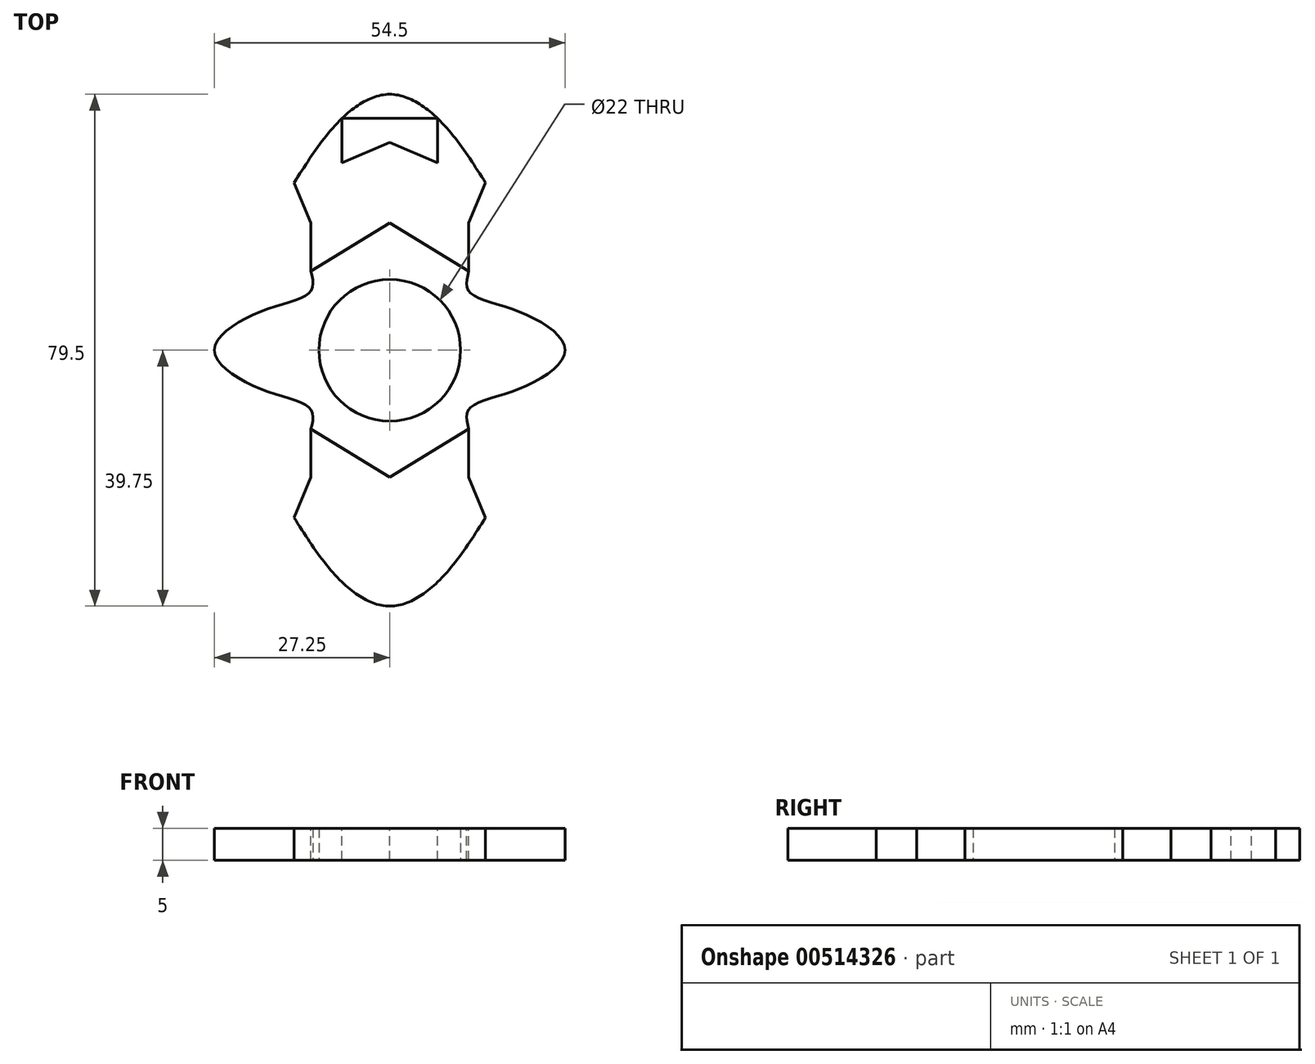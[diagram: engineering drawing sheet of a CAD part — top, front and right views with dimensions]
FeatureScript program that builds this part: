
annotation { "Feature Type Name" : "Feature", "Feature Type Description" : "" }
export const myFeature = defineFeature(function(context is Context, id is Id, definition is map)
    precondition{}
    {
        {
            var Q0;
            Q0=qCreatedBy(makeId("Top.planeOp"),FACE);
            var sketch = newSketch(context, id + "F0", { "sketchPlane" : qUnion([Q0])});
            skCircle(sketch, "E0", {"center": v(0, 0) * mm, "radius": 11 * mm});
            skCircle(sketch, "E1", {"center": v(0, 0) * mm, "radius": 12.25 * mm});
            skSolve(sketch);
        }
        {
            var Q0;
            Q0=qCreatedBy(makeId("Top.planeOp"),FACE);
            var sketch = newSketch(context, id + "F1", { "sketchPlane" : qUnion([Q0])});
            skLineSegment(sketch, "E2", {"start": v(0, 0) * mm, "end": v(-12.25, 0) * mm});
            skLineSegment(sketch, "E3", {"start": v(0, 0) * mm, "end": v(12.25, 0) * mm});
            skLineSegment(sketch, "E4", {"start": v(-12.25, 12.25) * mm, "end": v(0, 19.75) * mm});
            skLineSegment(sketch, "E5", {"start": v(0, 19.75) * mm, "end": v(12.25, 12.25) * mm});
            skLineSegment(sketch, "E6", {"start": v(-12.25, -12.25) * mm, "end": v(0, -19.75) * mm});
            skLineSegment(sketch, "E7", {"start": v(12.25, -12.25) * mm, "end": v(0, -19.75) * mm});
            skPoint(sketch, "E8.endSnap0", {"position": v(-12.25, 6.12) * mm});
            skPoint(sketch, "E9.endSnap0", {"position": v(-12.25, -6.12) * mm});
            skPoint(sketch, "E10.endSnap0", {"position": v(12.25, 6.12) * mm});
            skFitSpline(sketch, "E11", {"points": [v(-12.25, 12.25) * mm, v(-12.25, 9.19) * mm, v(-19.75, 6.12) * mm, v(-27.25, 0) * mm, v(-19.75, -6.12) * mm, v(-12.25, -9.19) * mm, v(-12.25, -12.25) * mm], "startDerivative": vector(7.59, -29.79) * mm, "endDerivative": vector(-7.59, -29.79) * mm});
            skFitSpline(sketch, "E12", {"points": [v(12.25, 12.25) * mm, v(12.25, 9.19) * mm, v(19.75, 6.12) * mm, v(27.25, 0) * mm, v(19.75, -6.12) * mm, v(12.25, -9.19) * mm, v(12.25, -12.25) * mm], "startDerivative": vector(-7.59, -29.79) * mm, "endDerivative": vector(7.59, -29.79) * mm});
            skLineSegment(sketch, "E13", {"start": v(-27.25, 0) * mm, "end": v(-12.25, 0) * mm});
            skLineSegment(sketch, "E14", {"start": v(-19.75, 0) * mm, "end": v(-12.25, 0) * mm});
            skLineSegment(sketch, "E15", {"start": v(12.25, 0) * mm, "end": v(27.25, 0) * mm});
            skLineSegment(sketch, "E16", {"start": v(19.75, 0) * mm, "end": v(12.25, 0) * mm});
            skSolve(sketch);
        }
        {
            var Q0;
            Q0=makeQuery(id+"F1.imprint","IMPRINT",FACE,{"disambiguationData":[TD([[makeQuery(id+"F1.imprint","IMPRINT",EDGE,{"derivedFrom":sQuery(id+"F1.wireOp",EDGE,"E2")}),-1.0]])]});
            var Q1;
            Q1=makeQuery(id+"F1.imprint","IMPRINT",FACE,{"disambiguationData":[TD([[makeQuery(id+"F1.imprint","IMPRINT",EDGE,{"derivedFrom":sQuery(id+"F1.wireOp",EDGE,"E2")}),1.0]])]});
            extrude(context, id + "F2", {"entities" : qUnion([Q0, Q1]), "depth" : 5 * mm, "offsetDistance" : 25 * mm});
        }
        {
            var Q0;
            Q0=makeQuery(id+"F0.imprint","IMPRINT",FACE,{"disambiguationData":[TD([[makeQuery(id+"F0.imprint","IMPRINT",EDGE,{"derivedFrom":sQuery(id+"F0.wireOp",EDGE,"E0")}),1.0]])]});
            extrude(context, id + "F3", {"entities" : qUnion([Q0]), "operationType" : NewBodyOperationType.REMOVE, "depth" : 25 * mm, "offsetDistance" : 25 * mm});
        }
        {
            var Q0;
            Q0=makeQuery(id+"F2.opExtrude","CAP_FACE",FACE,{"disambiguationData":[OSD([sQuery(id+"F1.wireOp",EDGE,"E4"),sQuery(id+"F1.wireOp",EDGE,"E5"),sQuery(id+"F1.wireOp",EDGE,"E6"),sQuery(id+"F1.wireOp",EDGE,"E7"),sQuery(id+"F1.wireOp",EDGE,"E11"),sQuery(id+"F1.wireOp",EDGE,"E12")])],"isStart":false});
            var sketch = newSketch(context, id + "F4", { "sketchPlane" : qUnion([Q0])});
            skLineSegment(sketch, "E17", {"start": v(-12.25, 12.25) * mm, "end": v(-12.25, 19.75) * mm});
            skLineSegment(sketch, "E18", {"start": v(12.25, 19.75) * mm, "end": v(12.25, 12.25) * mm});
            skLineSegment(sketch, "E19", {"start": v(0, 19.75) * mm, "end": v(0, 32.25) * mm});
            skLineSegment(sketch, "E20", {"start": v(-12.25, 19.75) * mm, "end": v(0, 32.25) * mm});
            skLineSegment(sketch, "E21", {"start": v(0, 32.25) * mm, "end": v(12.25, 19.75) * mm});
            skPoint(sketch, "E22.endSnap0", {"position": v(-6.12, 26) * mm});
            skLineSegment(sketch, "E23", {"start": v(-6.12, 26) * mm, "end": v(-14.88, 26) * mm});
            skLineSegment(sketch, "E24", {"start": v(6.12, 26) * mm, "end": v(14.88, 26) * mm});
            skLineSegment(sketch, "E25", {"start": v(-14.88, 26) * mm, "end": v(-6.12, 19.75) * mm});
            skLineSegment(sketch, "E26", {"start": v(14.88, 26) * mm, "end": v(6.12, 19.75) * mm});
            skLineSegment(sketch, "E27", {"start": v(-12.25, -12.25) * mm, "end": v(-12.25, -19.75) * mm});
            skLineSegment(sketch, "E28", {"start": v(12.25, -12.25) * mm, "end": v(12.25, -19.75) * mm});
            skLineSegment(sketch, "E29", {"start": v(0, -19.75) * mm, "end": v(0, -32.25) * mm});
            skLineSegment(sketch, "E30", {"start": v(-12.25, -19.75) * mm, "end": v(0, -32.25) * mm});
            skLineSegment(sketch, "E31", {"start": v(12.25, -19.75) * mm, "end": v(0, -32.25) * mm});
            skLineSegment(sketch, "E32", {"start": v(-6.12, -26) * mm, "end": v(-14.88, -26) * mm});
            skLineSegment(sketch, "E33", {"start": v(6.12, -26) * mm, "end": v(14.88, -26) * mm});
            skLineSegment(sketch, "E34", {"start": v(-14.88, -26) * mm, "end": v(-6.13, -19.75) * mm});
            skLineSegment(sketch, "E35", {"start": v(6.12, -19.75) * mm, "end": v(14.88, -26) * mm});
            skLineSegment(sketch, "E36", {"start": v(14.88, 26) * mm, "end": v(0, 32.25) * mm});
            skLineSegment(sketch, "E37", {"start": v(0, 32.25) * mm, "end": v(-14.88, 26) * mm});
            skLineSegment(sketch, "E38", {"start": v(14.88, 26) * mm, "end": v(12.25, 19.75) * mm});
            skLineSegment(sketch, "E39", {"start": v(-14.88, 26) * mm, "end": v(-12.25, 19.75) * mm});
            skLineSegment(sketch, "E40", {"start": v(12.25, -19.75) * mm, "end": v(14.88, -26) * mm});
            skLineSegment(sketch, "E41", {"start": v(14.88, -26) * mm, "end": v(0, -32.25) * mm});
            skLineSegment(sketch, "E42", {"start": v(0, -32.25) * mm, "end": v(-14.88, -26) * mm});
            skLineSegment(sketch, "E43", {"start": v(-14.88, -26) * mm, "end": v(-12.25, -19.75) * mm});
            skLineSegment(sketch, "E44", {"start": v(7.44, 29.12) * mm, "end": v(0, 32.25) * mm});
            skLineSegment(sketch, "E45", {"start": v(-7.44, 29.12) * mm, "end": v(0, 32.25) * mm});
            skLineSegment(sketch, "E46", {"start": v(0, 32.25) * mm, "end": v(0, 39.75) * mm});
            skLineSegment(sketch, "E47", {"start": v(0, -32.25) * mm, "end": v(0, -39.75) * mm});
            skLineSegment(sketch, "E48", {"start": v(7.44, -29.12) * mm, "end": v(7.44, -32.25) * mm});
            skLineSegment(sketch, "E49", {"start": v(-7.44, -29.12) * mm, "end": v(-7.44, -32.25) * mm});
            skLineSegment(sketch, "E50", {"start": v(7.44, 29.12) * mm, "end": v(7.44, 36) * mm});
            skPoint(sketch, "E50.endSnap0", {"position": v(0, 36) * mm});
            skLineSegment(sketch, "E51", {"start": v(7.44, 36) * mm, "end": v(0, 36) * mm});
            skLineSegment(sketch, "E52", {"start": v(-7.44, 29.12) * mm, "end": v(-7.44, 36) * mm});
            skLineSegment(sketch, "E53", {"start": v(-7.44, 36) * mm, "end": v(0, 36) * mm});
            skFitSpline(sketch, "E54", {"points": [v(14.88, 26) * mm, v(7.44, 36) * mm, v(0, 39.75) * mm, v(-7.44, 36) * mm, v(-14.88, 26) * mm], "startDerivative": vector(-25.38, 39.87) * mm, "endDerivative": vector(-25.38, -39.87) * mm});
            skLineSegment(sketch, "E55", {"start": v(0, -32.25) * mm, "end": v(0, -36) * mm});
            skLineSegment(sketch, "E56", {"start": v(0, -36) * mm, "end": v(7.44, -36) * mm});
            skLineSegment(sketch, "E57", {"start": v(7.44, -36) * mm, "end": v(7.44, -32.25) * mm});
            skLineSegment(sketch, "E58", {"start": v(0, -36) * mm, "end": v(-7.44, -36) * mm});
            skLineSegment(sketch, "E59", {"start": v(-7.44, -36) * mm, "end": v(-7.44, -32.25) * mm});
            skFitSpline(sketch, "E60", {"points": [v(14.88, -26) * mm, v(7.44, -36) * mm, v(0, -39.75) * mm, v(-7.44, -36) * mm, v(-14.88, -26) * mm], "startDerivative": vector(-25.38, -39.87) * mm, "endDerivative": vector(-25.38, 39.87) * mm});
            skSolve(sketch);
        }
        {
            var Q0;
            {var subQ3=sQuery(id+"F4.wireOp",EDGE,"E17");Q0=makeQuery(id+"F4.imprint","IMPRINT",FACE,{"disambiguationData":[TD([[makeQuery(id+"F4.imprint","IMPRINT",EDGE,{"derivedFrom":subQ3}),-1.0]])]});}
            var Q1;
            {var subQ4=sQuery(id+"F4.wireOp",EDGE,"E18");Q1=makeQuery(id+"F4.imprint","IMPRINT",FACE,{"disambiguationData":[TD([[makeQuery(id+"F4.imprint","IMPRINT",EDGE,{"derivedFrom":subQ4}),-1.0]])]});}
            var Q2;
            {var subQ0=sQuery(id+"F4.wireOp",EDGE,"E24");Q2=makeQuery(id+"F4.imprint","IMPRINT",FACE,{"disambiguationData":[TD([[makeQuery(id+"F4.imprint","IMPRINT",EDGE,{"derivedFrom":subQ0}),-1.0]])]});}
            var Q3;
            {var subQ0=sQuery(id+"F4.wireOp",EDGE,"E23");Q3=makeQuery(id+"F4.imprint","IMPRINT",FACE,{"disambiguationData":[TD([[makeQuery(id+"F4.imprint","IMPRINT",EDGE,{"derivedFrom":subQ0}),1.0]])]});}
            var Q4;
            {var subQ3=sQuery(id+"F4.wireOp",EDGE,"E27");Q4=makeQuery(id+"F4.imprint","IMPRINT",FACE,{"disambiguationData":[TD([[makeQuery(id+"F4.imprint","IMPRINT",EDGE,{"derivedFrom":subQ3}),1.0]])]});}
            var Q5;
            {var subQ4=sQuery(id+"F4.wireOp",EDGE,"E28");Q5=makeQuery(id+"F4.imprint","IMPRINT",FACE,{"disambiguationData":[TD([[makeQuery(id+"F4.imprint","IMPRINT",EDGE,{"derivedFrom":subQ4}),-1.0]])]});}
            var Q6;
            {var subQ0=sQuery(id+"F4.wireOp",EDGE,"E33");Q6=makeQuery(id+"F4.imprint","IMPRINT",FACE,{"disambiguationData":[TD([[makeQuery(id+"F4.imprint","IMPRINT",EDGE,{"derivedFrom":subQ0}),1.0]])]});}
            var Q7;
            {var subQ0=sQuery(id+"F4.wireOp",EDGE,"E32");Q7=makeQuery(id+"F4.imprint","IMPRINT",FACE,{"disambiguationData":[TD([[makeQuery(id+"F4.imprint","IMPRINT",EDGE,{"derivedFrom":subQ0}),-1.0]])]});}
            var Q8;
            {var subQ0=sQuery(id+"F4.wireOp",EDGE,"E38");Q8=makeQuery(id+"F4.imprint","IMPRINT",FACE,{"disambiguationData":[TD([[makeQuery(id+"F4.imprint","IMPRINT",EDGE,{"derivedFrom":subQ0}),-1.0]])]});}
            var Q9;
            {var subQ2=sQuery(id+"F4.wireOp",EDGE,"E33");Q9=makeQuery(id+"F4.imprint","IMPRINT",FACE,{"disambiguationData":[TD([[makeQuery(id+"F4.imprint","IMPRINT",EDGE,{"derivedFrom":subQ2}),-1.0]])]});}
            var Q10;
            {var subQ2=sQuery(id+"F4.wireOp",EDGE,"E23");Q10=makeQuery(id+"F4.imprint","IMPRINT",FACE,{"disambiguationData":[TD([[makeQuery(id+"F4.imprint","IMPRINT",EDGE,{"derivedFrom":subQ2}),-1.0]])]});}
            var Q11;
            {var subQ2=sQuery(id+"F4.wireOp",EDGE,"E24");Q11=makeQuery(id+"F4.imprint","IMPRINT",FACE,{"disambiguationData":[TD([[makeQuery(id+"F4.imprint","IMPRINT",EDGE,{"derivedFrom":subQ2}),1.0]])]});}
            var Q12;
            {var subQ2=sQuery(id+"F4.wireOp",EDGE,"E32");Q12=makeQuery(id+"F4.imprint","IMPRINT",FACE,{"disambiguationData":[TD([[makeQuery(id+"F4.imprint","IMPRINT",EDGE,{"derivedFrom":subQ2}),1.0]])]});}
            var Q13;
            {var subQ0=sQuery(id+"F4.wireOp",EDGE,"E43");Q13=makeQuery(id+"F4.imprint","IMPRINT",FACE,{"disambiguationData":[TD([[makeQuery(id+"F4.imprint","IMPRINT",EDGE,{"derivedFrom":subQ0}),-1.0]])]});}
            var Q14;
            {var subQ0=sQuery(id+"F4.wireOp",EDGE,"E40");Q14=makeQuery(id+"F4.imprint","IMPRINT",FACE,{"disambiguationData":[TD([[makeQuery(id+"F4.imprint","IMPRINT",EDGE,{"derivedFrom":subQ0}),-1.0]])]});}
            var Q15;
            {var subQ0=sQuery(id+"F4.wireOp",EDGE,"E39");Q15=makeQuery(id+"F4.imprint","IMPRINT",FACE,{"disambiguationData":[TD([[makeQuery(id+"F4.imprint","IMPRINT",EDGE,{"derivedFrom":subQ0}),1.0]])]});}
            var Q16;
            {var subQ0=sQuery(id+"F4.wireOp",EDGE,"E47");Q16=makeQuery(id+"F4.imprint","IMPRINT",FACE,{"disambiguationData":[TD([[makeQuery(id+"F4.imprint","IMPRINT",EDGE,{"derivedFrom":subQ0}),-1.0]])]});}
            var Q17;
            {var subQ0=sQuery(id+"F4.wireOp",EDGE,"E47");Q17=makeQuery(id+"F4.imprint","IMPRINT",FACE,{"disambiguationData":[TD([[makeQuery(id+"F4.imprint","IMPRINT",EDGE,{"derivedFrom":subQ0}),1.0]])]});}
            var Q18;
            {var subQ3=sQuery(id+"F4.wireOp",EDGE,"E48");Q18=makeQuery(id+"F4.imprint","IMPRINT",FACE,{"disambiguationData":[TD([[makeQuery(id+"F4.imprint","IMPRINT",EDGE,{"derivedFrom":subQ3}),1.0]])]});}
            var Q19;
            {var subQ3=sQuery(id+"F4.wireOp",EDGE,"E49");Q19=makeQuery(id+"F4.imprint","IMPRINT",FACE,{"disambiguationData":[TD([[makeQuery(id+"F4.imprint","IMPRINT",EDGE,{"derivedFrom":subQ3}),-1.0]])]});}
            var Q20;
            Q20=makeQuery(id+"F4.imprint","IMPRINT",FACE,{"disambiguationData":[TD([[makeQuery(id+"F4.imprint","IMPRINT",EDGE,{"derivedFrom":sQuery(id+"F4.wireOp",EDGE,"E45")}),1.0]])]});
            var Q21;
            Q21=makeQuery(id+"F4.imprint","IMPRINT",FACE,{"disambiguationData":[TD([[makeQuery(id+"F4.imprint","IMPRINT",EDGE,{"derivedFrom":sQuery(id+"F4.wireOp",EDGE,"E44")}),-1.0]])]});
            var Q22;
            {var subQ0=sQuery(id+"F4.wireOp",EDGE,"E36");Q22=makeQuery(id+"F4.imprint","IMPRINT",FACE,{"disambiguationData":[TD([[makeQuery(id+"F4.imprint","IMPRINT",EDGE,{"derivedFrom":subQ0}),-1.0]])]});}
            var Q23;
            {var subQ0=sQuery(id+"F4.wireOp",EDGE,"E37");Q23=makeQuery(id+"F4.imprint","IMPRINT",FACE,{"disambiguationData":[TD([[makeQuery(id+"F4.imprint","IMPRINT",EDGE,{"derivedFrom":subQ0}),-1.0]])]});}
            var Q24;
            {var subQ1=sQuery(id+"F4.wireOp",EDGE,"E49");Q24=makeQuery(id+"F4.imprint","IMPRINT",FACE,{"disambiguationData":[TD([[makeQuery(id+"F4.imprint","IMPRINT",EDGE,{"derivedFrom":subQ1}),1.0]])]});}
            var Q25;
            {var subQ1=sQuery(id+"F4.wireOp",EDGE,"E48");Q25=makeQuery(id+"F4.imprint","IMPRINT",FACE,{"disambiguationData":[TD([[makeQuery(id+"F4.imprint","IMPRINT",EDGE,{"derivedFrom":subQ1}),-1.0]])]});}
            var Q26;
            {var subQ3=sQuery(id+"F4.wireOp",EDGE,"E53");Q26=makeQuery(id+"F4.imprint","IMPRINT",FACE,{"disambiguationData":[TD([[makeQuery(id+"F4.imprint","IMPRINT",EDGE,{"derivedFrom":subQ3}),1.0]])]});}
            var Q27;
            {var subQ3=sQuery(id+"F4.wireOp",EDGE,"E51");Q27=makeQuery(id+"F4.imprint","IMPRINT",FACE,{"disambiguationData":[TD([[makeQuery(id+"F4.imprint","IMPRINT",EDGE,{"derivedFrom":subQ3}),-1.0]])]});}
            extrude(context, id + "F5", {"entities" : qUnion([Q0, Q1, Q2, Q3, Q4, Q5, Q6, Q7, Q8, Q9, Q10, Q11, Q12, Q13, Q14, Q15, Q16, Q17, Q18, Q19, Q20, Q21, Q22, Q23, Q24, Q25, Q26, Q27]), "oppositeDirection" : true, "depth" : 5 * mm, "offsetDistance" : 25 * mm});
        }
    });
